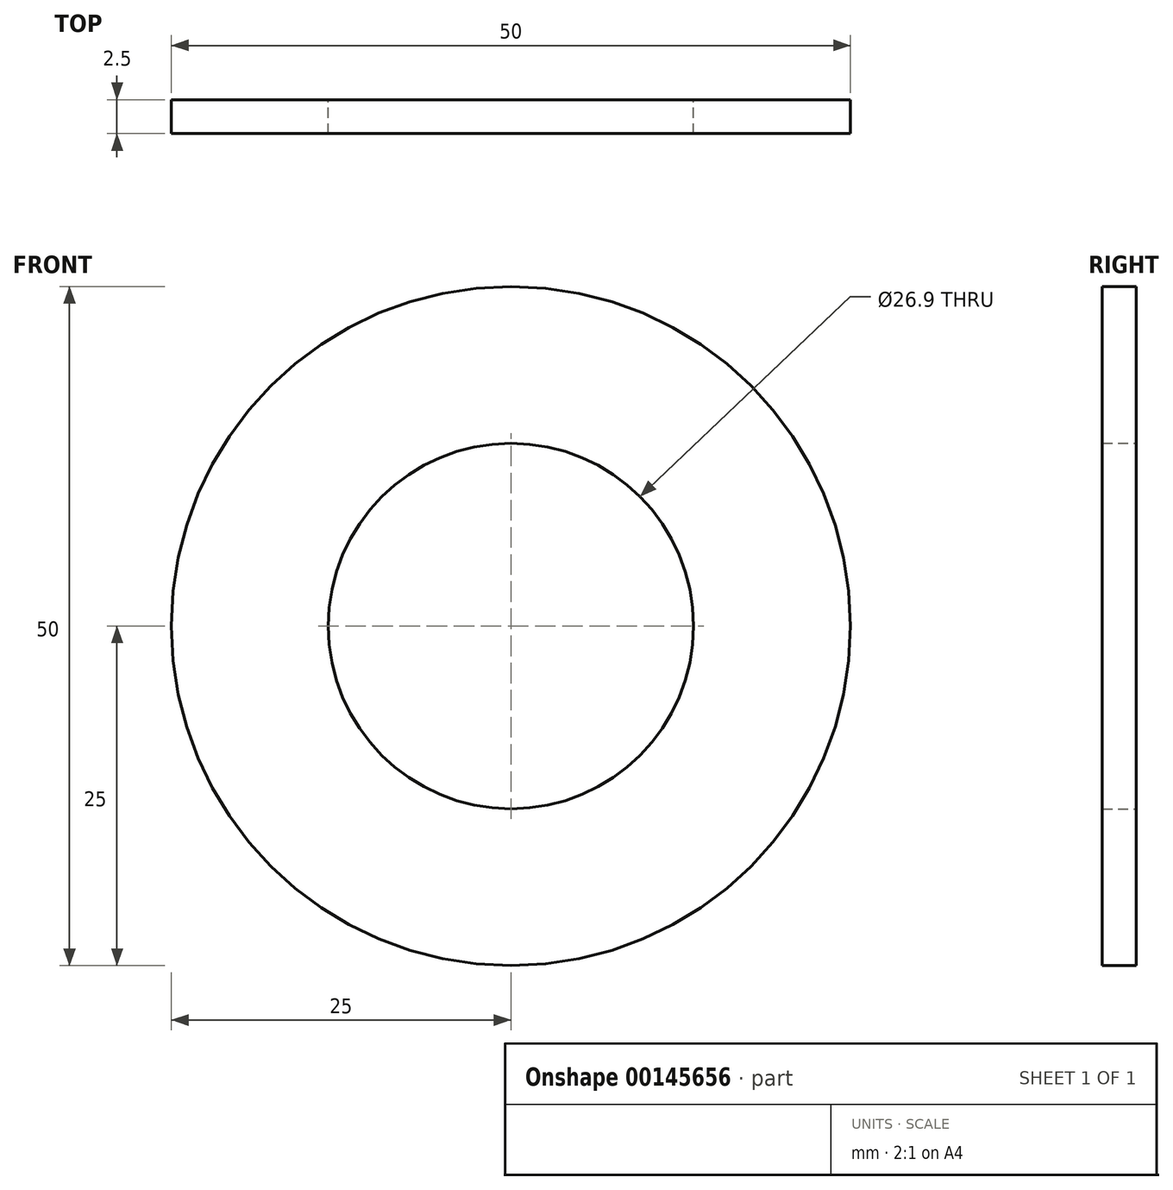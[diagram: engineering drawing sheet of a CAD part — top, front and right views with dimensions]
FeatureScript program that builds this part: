
annotation { "Feature Type Name" : "Feature", "Feature Type Description" : "" }
export const myFeature = defineFeature(function(context is Context, id is Id, definition is map)
    precondition{}
    {
        {
            var Q0;
            Q0=qCreatedBy(makeId("Front.planeOp"),FACE);
            var sketch = newSketch(context, id + "F0", { "sketchPlane" : qUnion([Q0])});
            skCircle(sketch, "E0", {"center": v(0, 0) * mm, "radius": 25 * mm});
            skCircle(sketch, "E1", {"center": v(0, 0) * mm, "radius": 13.45 * mm});
            skSolve(sketch);
        }
        {
            var Q0;
            Q0=makeQuery(id+"F0.imprint","IMPRINT",FACE,{"disambiguationData":[TD([[makeQuery(id+"F0.imprint","IMPRINT",EDGE,{"derivedFrom":sQuery(id+"F0.wireOp",EDGE,"E0")}),1.0]])]});
            extrude(context, id + "F1", {"entities" : qUnion([Q0]), "endBound" : BoundingType.SYMMETRIC, "depth" : 2.5 * mm});
        }
    });
